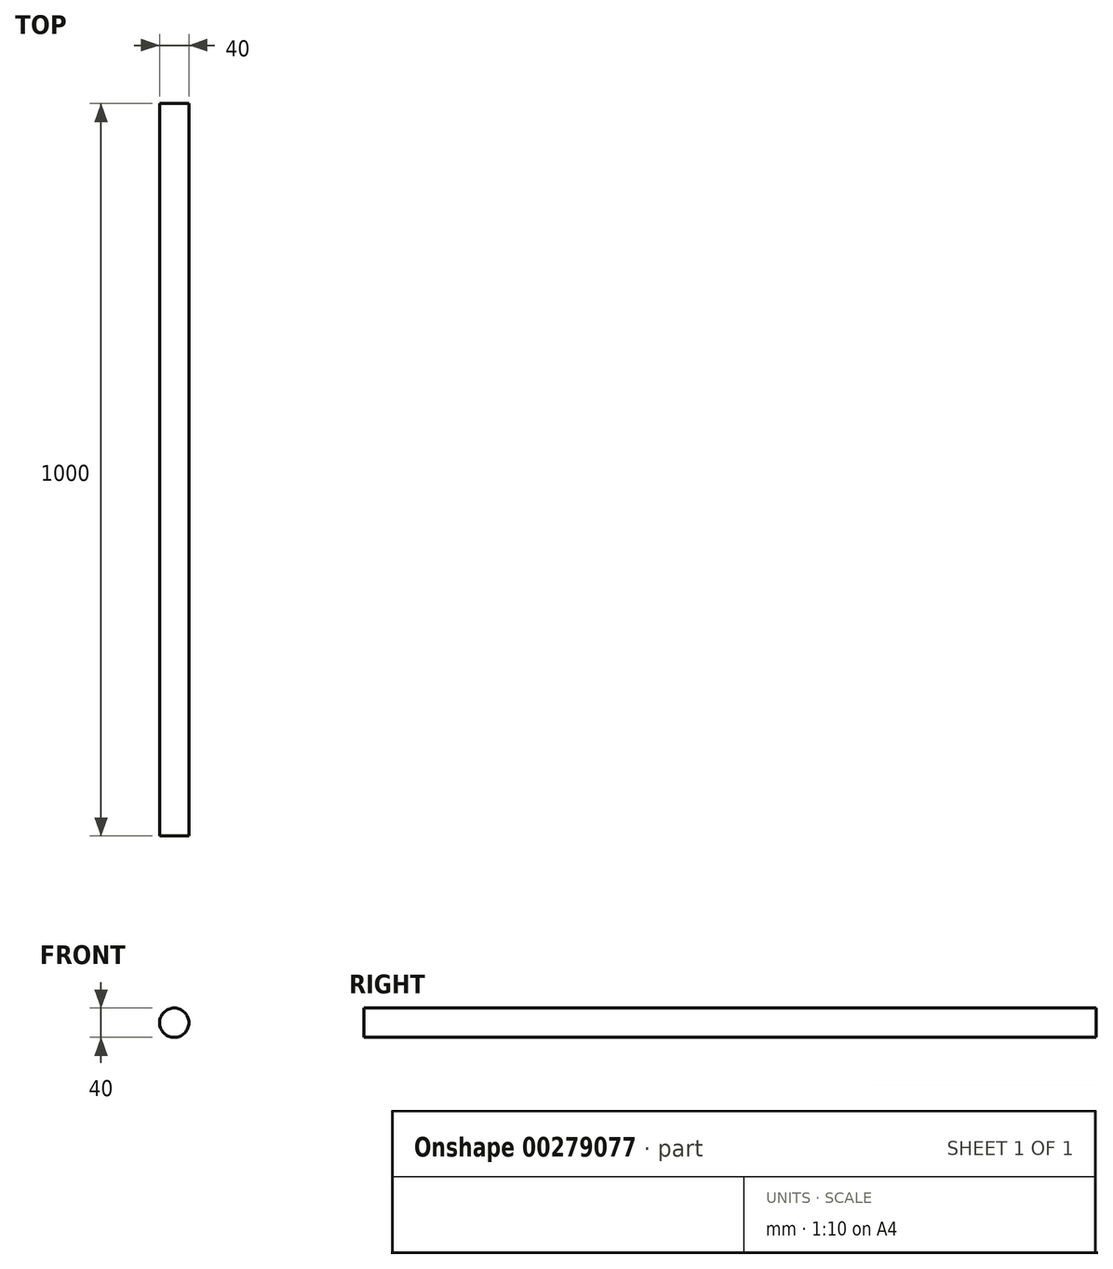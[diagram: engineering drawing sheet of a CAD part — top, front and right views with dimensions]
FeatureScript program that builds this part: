
annotation { "Feature Type Name" : "Feature", "Feature Type Description" : "" }
export const myFeature = defineFeature(function(context is Context, id is Id, definition is map)
    precondition{}
    {
        {
            var Q0;
            Q0=qCreatedBy(makeId("Front.planeOp"),FACE);
            var sketch = newSketch(context, id + "F0", { "sketchPlane" : qUnion([Q0])});
            skLineSegment(sketch, "E0", {"start": v(0, 0) * mm, "end": v(0, 300) * mm, "construction": true});
            skCircle(sketch, "E1", {"center": v(0, 300) * mm, "radius": 20 * mm});
            skSolve(sketch);
        }
        {
            var Q0;
            Q0 = qSketchRegion(id + "F0", true);
            extrude(context, id + "F1", {"entities" : qUnion([Q0]), "oppositeDirection" : true, "depth" : 1000 * mm});
        }
    });
